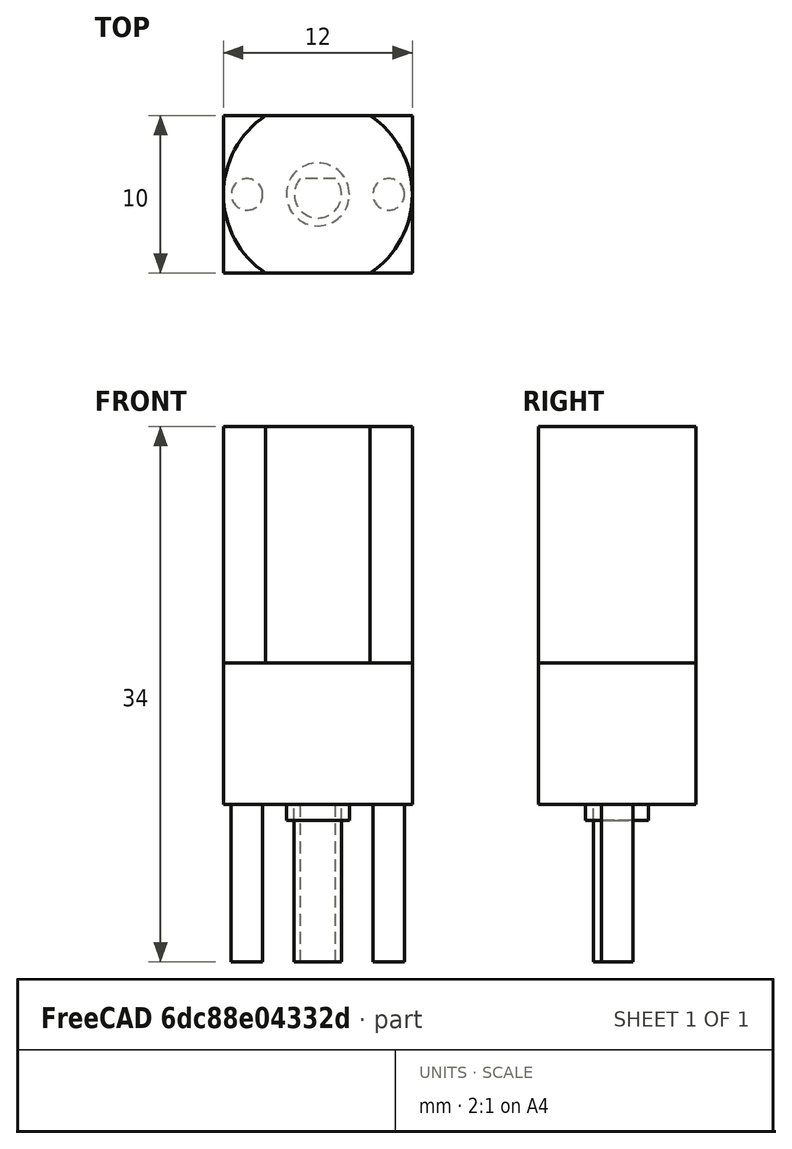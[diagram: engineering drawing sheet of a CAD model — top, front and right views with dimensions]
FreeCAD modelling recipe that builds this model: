
FCSTD DOCUMENT  (FreeCAD 0.18.4R)
Label: geared-motor
License: All rights reserved
LicenseURL: http://en.wikipedia.org/wiki/All_rights_reserved
objects: Part::Cylinder×8, Part::Box×6, Part::MultiCommon×2, Part::Cut×2, Part::MultiFuse×1
note: 19 computed .brp shape members not serialized (recipe doc carries the construction recipe); baked Part::Feature solids carry a one-line shape summary decoded from their .brp

FEATURE [Part::Cylinder] Cylinder031  label="shaft-1"
  Angle = 360
  AttacherType = Attacher::AttachEngine3D
  Height = 10
  Placement = pos=(0,0,-10) rot=(0,0,1;0rad)
  Radius = 1.5
FEATURE [Part::Cylinder] Cylinder032  label="screw-hole-1"
  Angle = 360
  AttacherType = Attacher::AttachEngine3D
  Height = 10
  Placement = pos=(4.5,0,-10) rot=(0,0,1;0rad)
  Radius = 1
FEATURE [Part::Cylinder] Cylinder033  label="screw-hole-2"
  Angle = 360
  AttacherType = Attacher::AttachEngine3D
  Height = 10
  Placement = pos=(-4.5,0,-10) rot=(0,0,1;0rad)
  Radius = 1
FEATURE [Part::Box] Box  label="gearbox"
  AttacherType = Attacher::AttachEngine3D
  Height = 9
  Length = 12
  Placement = pos=(-6,-5,0) rot=(0,0,1;0rad)
  Width = 10
FEATURE [Part::Cylinder] Cylinder034  label="boss"
  Angle = 360
  AttacherType = Attacher::AttachEngine3D
  Height = 1
  Placement = pos=(0,0,-1) rot=(0,0,1;0rad)
  Radius = 2
FEATURE [Part::Cylinder] Cylinder
  Angle = 360
  AttacherType = Attacher::AttachEngine3D
  Height = 15
  Placement = pos=(0,0,9) rot=(0,0,1;0rad)
  Radius = 6
FEATURE [Part::Box] Box001  label="gearbox001"
  AttacherType = Attacher::AttachEngine3D
  Height = 27
  Length = 16
  Placement = pos=(-8,-5,0) rot=(0,0,1;0rad)
  Width = 10
FEATURE [Part::Box] Box002  label="gearbox002"
  AttacherType = Attacher::AttachEngine3D
  Height = 9
  Length = 12
  Placement = pos=(-6,-5,0) rot=(0,0,1;0rad)
  Width = 10
FEATURE [Part::Box] Box003  label="gearbox003"
  AttacherType = Attacher::AttachEngine3D
  Height = 27
  Length = 16
  Placement = pos=(-8,-5,0) rot=(0,0,1;0rad)
  Width = 10
FEATURE [Part::Cylinder] Cylinder036  label="boss001"
  Angle = 360
  AttacherType = Attacher::AttachEngine3D
  Height = 1
  Placement = pos=(0,0,-1) rot=(0,0,1;0rad)
  Radius = 2
FEATURE [Part::Cylinder] Cylinder037
  Angle = 360
  AttacherType = Attacher::AttachEngine3D
  Height = 15
  Placement = pos=(0,0,9) rot=(0,0,1;0rad)
  Radius = 6
FEATURE [Part::MultiCommon] Common001  label="motor001"
  Shapes = -> [Cylinder037,Box003]
FEATURE [Part::Box] Box004  label="Cube"
  AttacherType = Attacher::AttachEngine3D
  Height = 12
  Length = 10
  Placement = pos=(-5,1,-11) rot=(0,0,1;0rad)
  Width = 10
FEATURE [Part::Cut] Cut  label="shaft"
  Base = -> Cylinder031
  Tool = -> Box004
FEATURE [Part::Cylinder] Cylinder038  label="shaft-002"
  Angle = 360
  AttacherType = Attacher::AttachEngine3D
  Height = 10
  Placement = pos=(0,0,-10) rot=(0,0,1;0rad)
  Radius = 1.5
FEATURE [Part::Box] Box005  label="Cube001"
  AttacherType = Attacher::AttachEngine3D
  Height = 12
  Length = 10
  Placement = pos=(-5,1,-11) rot=(0,0,1;0rad)
  Width = 10
FEATURE [Part::Cut] Cut001  label="shaft001"
  Base = -> Cylinder038
  Tool = -> Box005
FEATURE [Part::MultiCommon] Common  label="motor"
  Shapes = -> [Box001,Cylinder]
FEATURE [Part::MultiFuse] Fusion  label="motor-assembled"
  Shapes = -> [Box002,Cylinder036,Common001,Cut001]
